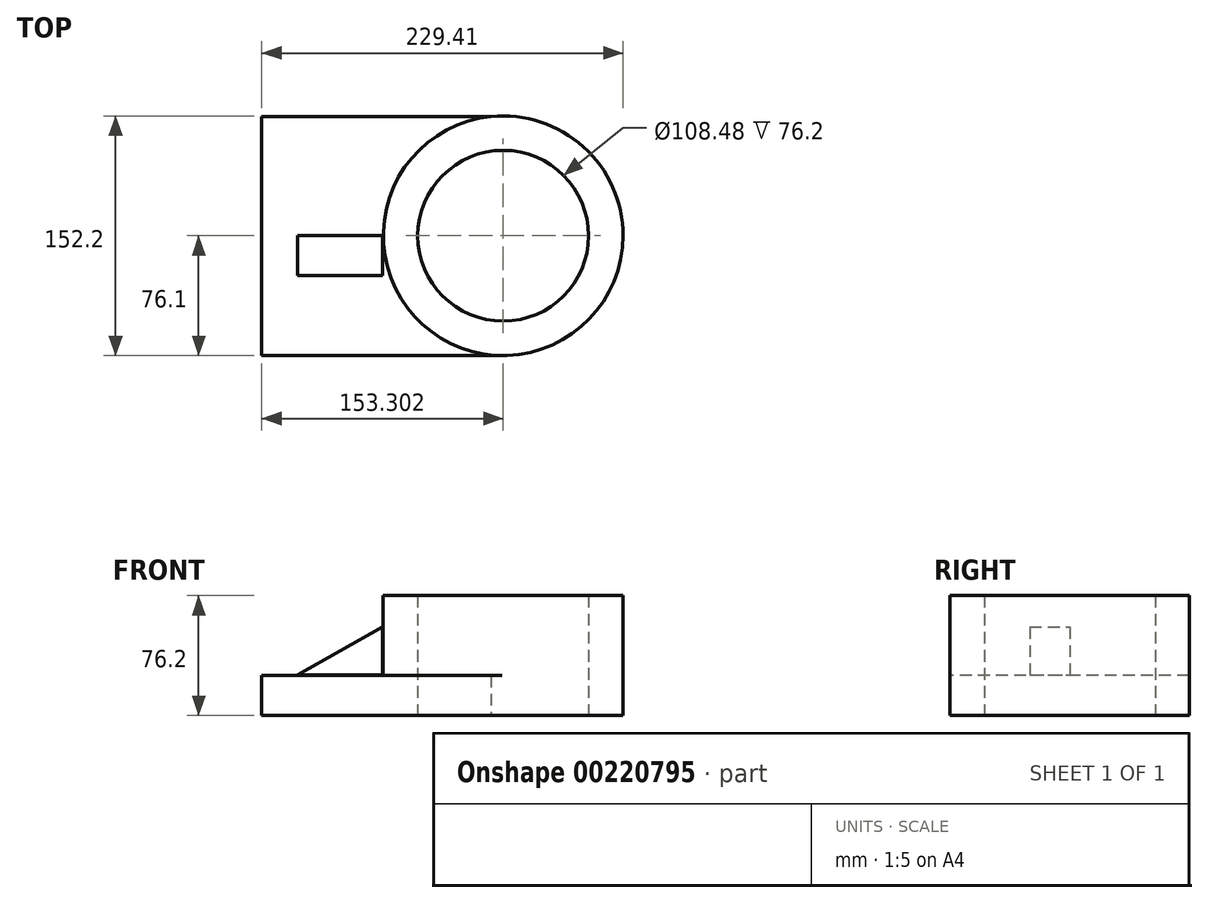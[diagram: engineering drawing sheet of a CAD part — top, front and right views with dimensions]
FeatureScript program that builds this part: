
annotation { "Feature Type Name" : "Feature", "Feature Type Description" : "" }
export const myFeature = defineFeature(function(context is Context, id is Id, definition is map)
    precondition{}
    {
        {
            var Q0;
            Q0=qCreatedBy(makeId("Top.planeOp"),FACE);
            var sketch = newSketch(context, id + "F0", { "sketchPlane" : qUnion([Q0])});
            skLineSegment(sketch, "E0.bottom", {"start": v(-76.72, 75.73) * mm, "end": v(76.58, 75.73) * mm});
            skLineSegment(sketch, "E0.top", {"start": v(-76.72, -76.1) * mm, "end": v(76.58, -76.1) * mm});
            skLineSegment(sketch, "E0.left", {"start": v(-76.72, 75.73) * mm, "end": v(-76.72, -76.1) * mm});
            skLineSegment(sketch, "E0.right", {"start": v(76.58, 75.73) * mm, "end": v(76.58, -76.1) * mm});
            skCircle(sketch, "E1", {"center": v(76.58, 0) * mm, "radius": 76.1 * mm});
            skCircle(sketch, "E2", {"center": v(76.58, 0) * mm, "radius": 54.24 * mm});
            skSolve(sketch);
        }
        {
            var Q0;
            {var subQ0=sQuery(id+"F0.wireOp",EDGE,"E0.right");var subQ5=sQuery(id+"F0.wireOp",EDGE,"E0.bottom");var subQ6=makeQuery(id+"F0.imprint","INTERSECT",VERTEX,{"derivedFrom":[subQ5,subQ0]});Q0=makeQuery(id+"F0.imprint","IMPRINT",FACE,{"disambiguationData":[TD([[makeQuery(id+"F0.imprint","IMPRINT",EDGE,{"disambiguationData":[TD([[subQ6,1.0]])],"derivedFrom":subQ5}),-1.0]])]});}
            var Q1;
            {var subQ0=sQuery(id+"F0.wireOp",EDGE,"E0.right");var subQ5=sQuery(id+"F0.wireOp",EDGE,"E0.bottom");var subQ6=makeQuery(id+"F0.imprint","INTERSECT",VERTEX,{"derivedFrom":[subQ5,subQ0]});Q1=makeQuery(id+"F0.imprint","IMPRINT",FACE,{"disambiguationData":[TD([[makeQuery(id+"F0.imprint","IMPRINT",EDGE,{"disambiguationData":[TD([[subQ6,1.0]])],"derivedFrom":subQ5}),1.0]])]});}
            extrude(context, id + "F1", {"entities" : qUnion([Q0, Q1]), "depth" : 76.2 * mm});
        }
        {
            var Q0;
            Q0 = qSketchRegion(id + "F0", true);
            extrude(context, id + "F2", {"entities" : qUnion([Q0]), "operationType" : NewBodyOperationType.ADD, "depth" : 25.4 * mm});
        }
        {
            var Q0;
            Q0=qCreatedBy(makeId("Front.planeOp"),FACE);
            var sketch = newSketch(context, id + "F3", { "sketchPlane" : qUnion([Q0])});
            skLineSegment(sketch, "E3.bottom", {"start": v(0, 56.23) * mm, "end": v(-53.92, 56.23) * mm});
            skLineSegment(sketch, "E3.top", {"start": v(0, 25.75) * mm, "end": v(-53.92, 25.75) * mm});
            skLineSegment(sketch, "E3.left", {"start": v(0, 56.23) * mm, "end": v(0, 25.75) * mm});
            skLineSegment(sketch, "E3.right", {"start": v(-53.92, 56.23) * mm, "end": v(-53.92, 25.75) * mm});
            skSolve(sketch);
        }
        {
            var Q0;
            Q0=makeQuery(id+"F3.imprint","IMPRINT",FACE,{"disambiguationData":[TD([[makeQuery(id+"F3.imprint","IMPRINT",EDGE,{"derivedFrom":sQuery(id+"F3.wireOp",EDGE,"E3.bottom")}),1.0]])]});
            extrude(context, id + "F4", {"entities" : qUnion([Q0]), "depth" : 25.4 * mm});
        }
        {
            var Q0;
            Q0=makeQuery(id+"F4.opExtrude","CAP_FACE",FACE,{"disambiguationData":[OSD([sQuery(id+"F3.wireOp",EDGE,"E3.bottom"),sQuery(id+"F3.wireOp",EDGE,"E3.top"),sQuery(id+"F3.wireOp",EDGE,"E3.left"),sQuery(id+"F3.wireOp",EDGE,"E3.right")])],"isStart":false});
            var sketch = newSketch(context, id + "F5", { "sketchPlane" : qUnion([Q0])});
            skLineSegment(sketch, "E4", {"start": v(0, 56.23) * mm, "end": v(-53.92, 25.75) * mm});
            skSolve(sketch);
        }
        {
            var Q0;
            Q0=makeQuery(id+"F5.imprint","IMPRINT",FACE,{"disambiguationData":[TD([[makeQuery(id+"F5.imprint","IMPRINT",EDGE,{"derivedFrom":sQuery(id+"F5.wireOp",EDGE,"E4")}),-1.0]])]});
            extrude(context, id + "F6", {"entities" : qUnion([Q0]), "operationType" : NewBodyOperationType.REMOVE, "oppositeDirection" : true, "depth" : 76.2 * mm});
        }
    });
